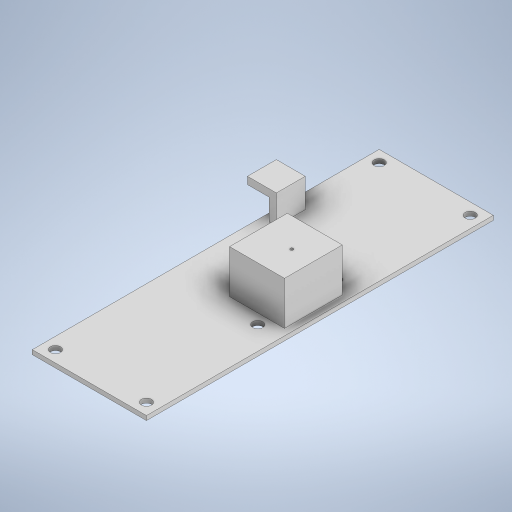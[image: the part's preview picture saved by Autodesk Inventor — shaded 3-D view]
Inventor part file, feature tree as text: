
AUTODESK INVENTOR PART (.ipt)
format: ipt  version: 2023 (Build 270158000, 158)  size: 343,040 bytes
history: native  units: mm
features: extrude x12, sketch x12
ambient origin geometry x8: Origin, YZ Plane, XZ Plane, XY Plane, X Axis, Y Axis, Z Axis, Center Point
bodies: Body1 (feature_tree)
feature tree (24):
  extrude  "Extrusion33"  Depth=240.0mm
  extrude  "Extrusion34"  Depth=38.0mm
  extrude  "Extrusion35"  Depth=30.0mm TaperAngle=0.0deg
  extrude  "Extrusion38"  Depth=30.0mm
  extrude  "Extrusion39"  Depth=15.0mm
  extrude  "Extrusion40"  Depth=3.2mm
  extrude  "Extrusion41"  Depth=35.0mm TaperAngle=0.0deg
  extrude  "Extrusion42"  Depth=20.0mm
  extrude  "Extrusion43"  Depth=20.0mm
  extrude  "Extrusion46"  Depth=5.0mm TaperAngle=0.0deg
  extrude  "Extrusion47"  TaperAngle=0.0deg  [1 undecoded]
  extrude  "Extrusion48"  Depth=10.0mm TaperAngle=0.0deg
  sketch  "Sketch44"  dims[d138=79.0mm d139=240.0mm]
  sketch  "Sketch45"  dims[d140=3.0mm d141=0.0mm d142=38.0mm]
  sketch  "Sketch47"  dims[d143=40.0mm d144=30.0mm d145=0.0mm]
  sketch  "Sketch58"  dims[d146=36.0mm d147=30.0mm d148=-2.617994mm]
  sketch  "Sketch59"  dims[d156=20.0mm d157=15.0mm]
  sketch  "Sketch60"  dims[d158=15.0mm d159=0.0mm d160=3.2mm]
  sketch  "Sketch61"  dims[d161=20.0mm d162=35.0mm d163=0.0mm]
  sketch  "Sketch64"  dims[d164=5.0mm d165=20.0mm]
  sketch  "Sketch65"  dims[d166=20.0mm d167=0.0mm d168=20.0mm]
  sketch  "Sketch68"  dims[d169=20.0mm d170=5.0mm d171=0.0mm]
  sketch  "Sketch69"  dims[d173=2.0mm d174=0.0mm d175=0.0mm]
  sketch  "Sketch70"  dims[d176=6.0mm d177=10.0mm d178=0.0mm d192=7.0mm d193=7.0mm d194=7.0mm d195=7.0mm d196=10.0mm d197=0.0mm d198=7.0mm d199=7.0mm d200=10.0mm d201=0.0mm d202=8.0mm d203=0.0mm d49=0.5mm d50=0.872665mm d51=0.5mm d52=0.872665mm d130=0.5mm d131=0.872665mm d132=0.5mm d133=0.872665mm]
note: 1 required parameter value undecoded (feature->parameter linkage not recoverable at this tier; creation-order binding heuristic only, values carry confidence <= 0.55)
